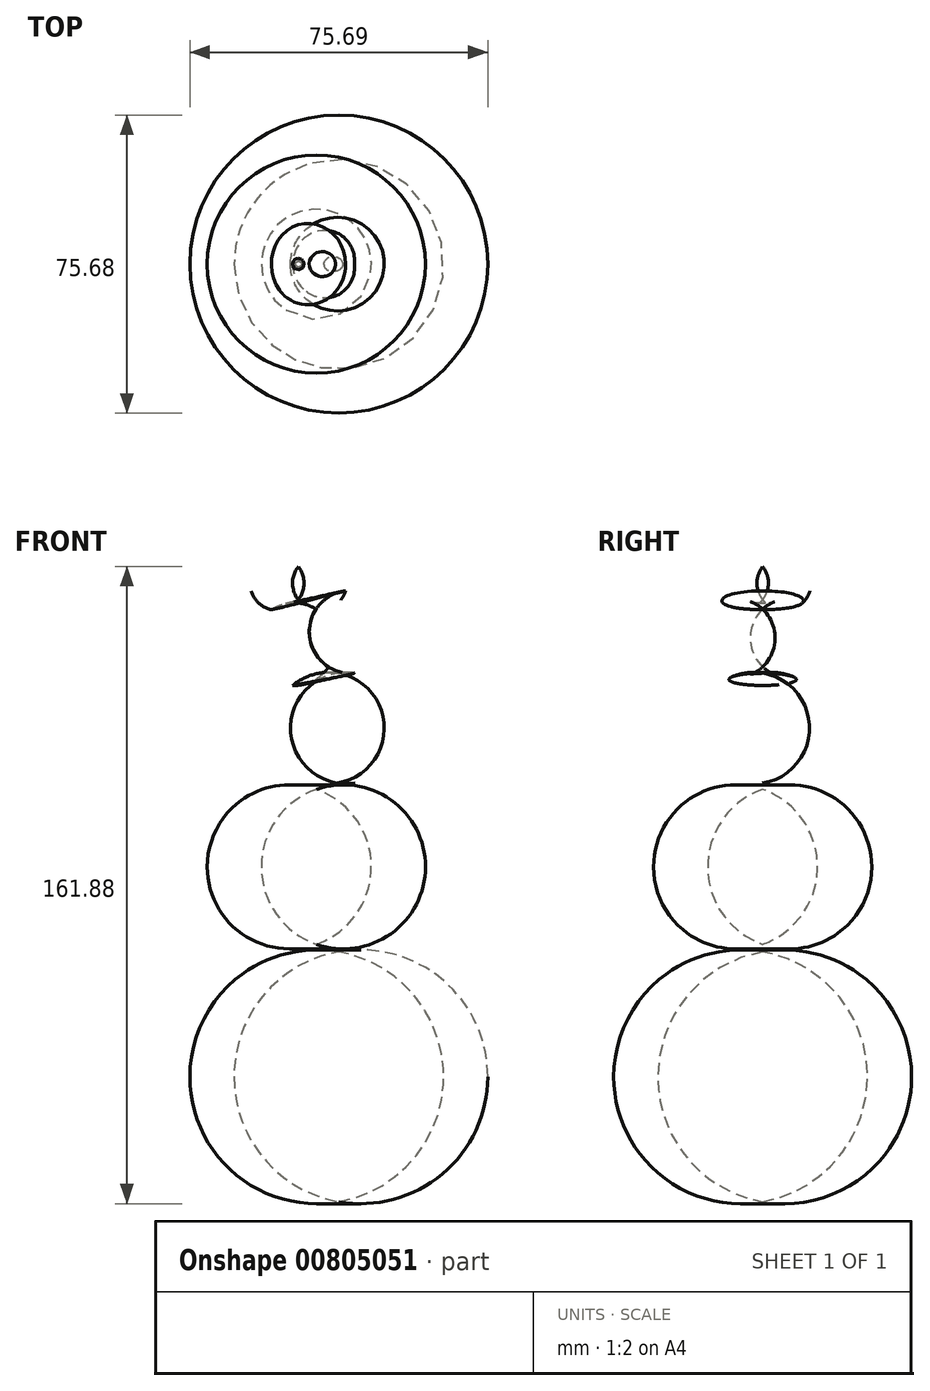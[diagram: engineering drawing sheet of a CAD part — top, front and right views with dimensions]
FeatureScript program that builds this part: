
annotation { "Feature Type Name" : "Feature", "Feature Type Description" : "" }
export const myFeature = defineFeature(function(context is Context, id is Id, definition is map)
    precondition{}
    {
        {
            var Q0;
            Q0=qCreatedBy(makeId("Front.planeOp"),FACE);
            var sketch = newSketch(context, id + "F0", { "sketchPlane" : qUnion([Q0])});
            skLineSegment(sketch, "E0", {"start": v(-3, -15.31) * mm, "end": v(-3, -78.81) * mm});
            skArc(sketch, "E1", {"start": v(-3, -78.81) * mm, "mid": v(34.85, -47.06) * mm, "end": v(-3, -15.31) * mm});
            skSolve(sketch);
        }
        {
            var Q0;
            Q0 = qSketchRegion(id + "F0", true);
            var Q1;
            Q1=sQuery(id+"F0.wireOp",EDGE,"E0");
            revolve(context, id + "F1", {"surfaceOperationType" : NewSurfaceOperationType.NEW, "entities" : qUnion([Q0]), "axis" : qUnion([Q1]), "revolveType" : RevolveType.FULL});
        }
        {
            var Q0;
            Q0=qCreatedBy(makeId("Front.planeOp"),FACE);
            var sketch = newSketch(context, id + "F2", { "sketchPlane" : qUnion([Q0])});
            skLineSegment(sketch, "E2", {"start": v(-8.7, 25.96) * mm, "end": v(-8.7, -13.4) * mm});
            skArc(sketch, "E3", {"start": v(-8.7, -13.4) * mm, "mid": v(19.02, 6.28) * mm, "end": v(-8.7, 25.96) * mm});
            skSolve(sketch);
        }
        {
            var Q0;
            Q0 = qSketchRegion(id + "F2", true);
            var Q1;
            Q1=sQuery(id+"F2.wireOp",EDGE,"E2");
            revolve(context, id + "F3", {"surfaceOperationType" : NewSurfaceOperationType.NEW, "entities" : qUnion([Q0]), "axis" : qUnion([Q1]), "revolveType" : RevolveType.FULL});
        }
        {
            var Q0;
            Q0=qCreatedBy(makeId("Front.planeOp"),FACE);
            var sketch = newSketch(context, id + "F4", { "sketchPlane" : qUnion([Q0])});
            skLineSegment(sketch, "E4", {"start": v(-3.35, 55.5) * mm, "end": v(-3.35, 27.55) * mm});
            skArc(sketch, "E5", {"start": v(-3.35, 27.55) * mm, "mid": v(13.05, 41.52) * mm, "end": v(-3.35, 55.5) * mm});
            skSolve(sketch);
        }
        {
            var Q0;
            Q0 = qSketchRegion(id + "F4", true);
            var Q1;
            Q1=sQuery(id+"F4.wireOp",EDGE,"E4");
            revolve(context, id + "F5", {"surfaceOperationType" : NewSurfaceOperationType.NEW, "entities" : qUnion([Q0]), "axis" : qUnion([Q1]), "revolveType" : RevolveType.FULL});
        }
        {
            var Q0;
            Q0=qCreatedBy(makeId("Front.planeOp"),FACE);
            var sketch = newSketch(context, id + "F6", { "sketchPlane" : qUnion([Q0])});
            skLineSegment(sketch, "E6", {"start": v(-8.75, 71.75) * mm, "end": v(-5.57, 57.06) * mm});
            skArc(sketch, "E7", {"start": v(-5.57, 57.06) * mm, "mid": v(10.29, 68.19) * mm, "end": v(-8.75, 71.75) * mm});
            skSolve(sketch);
        }
        {
            var Q0;
            Q0 = qSketchRegion(id + "F6", true);
            var Q1;
            Q1=sQuery(id+"F6.wireOp",EDGE,"E6");
            revolve(context, id + "F7", {"operationType" : NewBodyOperationType.ADD, "surfaceOperationType" : NewSurfaceOperationType.NEW, "entities" : qUnion([Q0]), "axis" : qUnion([Q1]), "revolveType" : RevolveType.FULL});
        }
        {
            var Q0;
            Q0=qCreatedBy(makeId("Front.planeOp"),FACE);
            var sketch = newSketch(context, id + "F8", { "sketchPlane" : qUnion([Q0])});
            skLineSegment(sketch, "E8", {"start": v(-13.28, 82.57) * mm, "end": v(-13.28, 74.12) * mm});
            skArc(sketch, "E9", {"start": v(-13.28, 74.12) * mm, "mid": v(-1, 78.35) * mm, "end": v(-13.28, 82.57) * mm});
            skSolve(sketch);
        }
        {
            var Q0;
            Q0 = qSketchRegion(id + "F8", true);
            var Q1;
            Q1=sQuery(id+"F8.wireOp",EDGE,"E8");
            revolve(context, id + "F9", {"operationType" : NewBodyOperationType.ADD, "surfaceOperationType" : NewSurfaceOperationType.NEW, "entities" : qUnion([Q0]), "axis" : qUnion([Q1]), "revolveType" : RevolveType.FULL});
        }
    });
